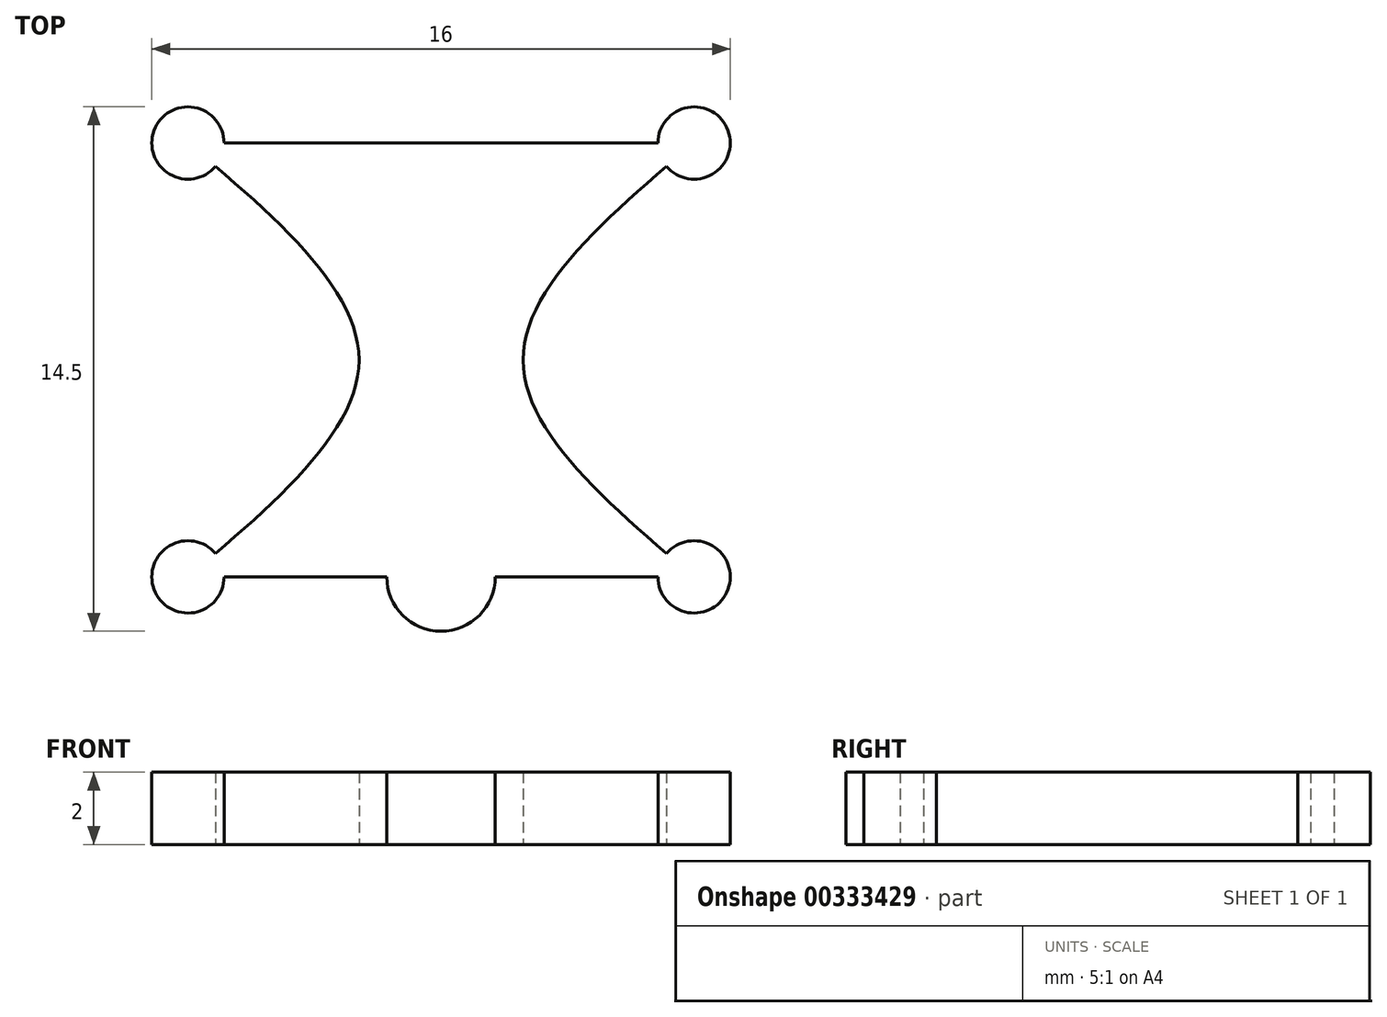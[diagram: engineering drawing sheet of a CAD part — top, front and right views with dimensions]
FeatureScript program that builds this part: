
annotation { "Feature Type Name" : "Feature", "Feature Type Description" : "" }
export const myFeature = defineFeature(function(context is Context, id is Id, definition is map)
    precondition{}
    {
        {
            var Q0;
            Q0=qCreatedBy(makeId("Top.planeOp"),FACE);
            var sketch = newSketch(context, id + "F0", { "sketchPlane" : qUnion([Q0])});
            skLineSegment(sketch, "E0", {"start": v(-7, 0) * mm, "end": v(7, 0) * mm});
            skArc(sketch, "E1", {"start": v(-1.5, 0) * mm, "mid": v(0, 1.5) * mm, "end": v(1.5, 0) * mm});
            skLineSegment(sketch, "E2", {"start": v(0, 0) * mm, "end": v(0, -12) * mm});
            skLineSegment(sketch, "E3", {"start": v(-7, -12) * mm, "end": v(7, -12) * mm});
            skPoint(sketch, "E4", {"position": v(0, -6) * mm});
            skLineSegment(sketch, "E5", {"start": v(-2.27, -6) * mm, "end": v(2.27, -6) * mm});
            skFitSpline(sketch, "E6", {"points": [v(-7, -12) * mm, v(-2.27, -6) * mm, v(-7, 0) * mm], "startDerivative": vector(14.2, 12) * mm, "endDerivative": vector(-14.2, 12) * mm});
            skFitSpline(sketch, "E7", {"points": [v(7, -12) * mm, v(2.27, -6) * mm, v(7, 0) * mm], "startDerivative": vector(-14.2, 12) * mm, "endDerivative": vector(14.2, 12) * mm});
            skCircle(sketch, "E8", {"center": v(-7, 0) * mm, "radius": 1 * mm});
            skCircle(sketch, "E9", {"center": v(-7, -12) * mm, "radius": 1 * mm});
            skCircle(sketch, "E10.MirrorC", {"center": v(7, 0) * mm, "radius": 1 * mm});
            skCircle(sketch, "E11.MirrorC", {"center": v(7, -12) * mm, "radius": 1 * mm});
            skArc(sketch, "E12", {"start": v(-1.5, -12) * mm, "mid": v(0, -13.5) * mm, "end": v(1.5, -12) * mm});
            skSolve(sketch);
        }
        {
            var Q0;
            {var subQ0=sQuery(id+"F0.wireOp",EDGE,"E6");var subQ1=sQuery(id+"F0.wireOp",EDGE,"E0");var subQ2=makeQuery(id+"F0.imprint","INTERSECT",VERTEX,{"derivedFrom":[subQ1,subQ0]});Q0=makeQuery(id+"F0.imprint","IMPRINT",FACE,{"disambiguationData":[TD([[makeQuery(id+"F0.imprint","IMPRINT",EDGE,{"disambiguationData":[TD([[subQ2,-1.0]])],"derivedFrom":subQ1}),1.0]])]});}
            var Q1;
            {var subQ0=sQuery(id+"F0.wireOp",EDGE,"E6");var subQ1=sQuery(id+"F0.wireOp",EDGE,"E0");var subQ2=makeQuery(id+"F0.imprint","INTERSECT",VERTEX,{"derivedFrom":[subQ1,subQ0]});Q1=makeQuery(id+"F0.imprint","IMPRINT",FACE,{"disambiguationData":[TD([[makeQuery(id+"F0.imprint","IMPRINT",EDGE,{"disambiguationData":[TD([[subQ2,-1.0]])],"derivedFrom":subQ1}),-1.0]])]});}
            var Q2;
            {var subQ6=sQuery(id+"F0.wireOp",EDGE,"E0");var subQ10=makeQuery(id+"F0.imprint","INTERSECT",VERTEX,{"disambiguationData":[OD(0.0)],"derivedFrom":[subQ6,sQuery(id+"F0.wireOp",EDGE,"E1")]});Q2=makeQuery(id+"F0.imprint","IMPRINT",FACE,{"disambiguationData":[TD([[makeQuery(id+"F0.imprint","IMPRINT",EDGE,{"disambiguationData":[TD([[subQ10,1.0]])],"derivedFrom":subQ6}),-1.0]])]});}
            var Q3;
            {var subQ0=sQuery(id+"F0.wireOp",EDGE,"E1");Q3=makeQuery(id+"F0.imprint","IMPRINT",FACE,{"disambiguationData":[TD([[makeQuery(id+"F0.imprint","IMPRINT",EDGE,{"derivedFrom":subQ0}),-1.0]])]});}
            var Q4;
            {var subQ5=sQuery(id+"F0.wireOp",EDGE,"E0");var subQ7=makeQuery(id+"F0.imprint","INTERSECT",VERTEX,{"disambiguationData":[OD(1.0)],"derivedFrom":[subQ5,sQuery(id+"F0.wireOp",EDGE,"E1")]});Q4=makeQuery(id+"F0.imprint","IMPRINT",FACE,{"disambiguationData":[TD([[makeQuery(id+"F0.imprint","IMPRINT",EDGE,{"disambiguationData":[TD([[subQ7,1.0]])],"derivedFrom":subQ5}),-1.0]])]});}
            var Q5;
            {var subQ0=sQuery(id+"F0.wireOp",EDGE,"E7");var subQ1=sQuery(id+"F0.wireOp",EDGE,"E0");var subQ2=makeQuery(id+"F0.imprint","INTERSECT",VERTEX,{"derivedFrom":[subQ1,subQ0]});Q5=makeQuery(id+"F0.imprint","IMPRINT",FACE,{"disambiguationData":[TD([[makeQuery(id+"F0.imprint","IMPRINT",EDGE,{"disambiguationData":[TD([[subQ2,1.0]])],"derivedFrom":subQ1}),-1.0]])]});}
            var Q6;
            {var subQ0=sQuery(id+"F0.wireOp",EDGE,"E7");var subQ1=sQuery(id+"F0.wireOp",EDGE,"E0");var subQ2=makeQuery(id+"F0.imprint","INTERSECT",VERTEX,{"derivedFrom":[subQ1,subQ0]});Q6=makeQuery(id+"F0.imprint","IMPRINT",FACE,{"disambiguationData":[TD([[makeQuery(id+"F0.imprint","IMPRINT",EDGE,{"disambiguationData":[TD([[subQ2,1.0]])],"derivedFrom":subQ1}),1.0]])]});}
            var Q7;
            {var subQ0=sQuery(id+"F0.wireOp",EDGE,"E3");var subQ1=sQuery(id+"F0.wireOp",EDGE,"E2");var subQ2=makeQuery(id+"F0.imprint","INTERSECT",VERTEX,{"derivedFrom":[subQ1,subQ0]});Q7=makeQuery(id+"F0.imprint","IMPRINT",FACE,{"disambiguationData":[TD([[makeQuery(id+"F0.imprint","IMPRINT",EDGE,{"disambiguationData":[TD([[subQ2,1.0]])],"derivedFrom":subQ1}),-1.0]])]});}
            var Q8;
            {var subQ3=sQuery(id+"F0.wireOp",EDGE,"E2");var subQ5=sQuery(id+"F0.wireOp",EDGE,"E3");var subQ6=makeQuery(id+"F0.imprint","INTERSECT",VERTEX,{"derivedFrom":[subQ3,subQ5]});Q8=makeQuery(id+"F0.imprint","IMPRINT",FACE,{"disambiguationData":[TD([[makeQuery(id+"F0.imprint","IMPRINT",EDGE,{"disambiguationData":[TD([[subQ6,1.0]])],"derivedFrom":subQ3}),1.0]])]});}
            var Q9;
            {var subQ0=sQuery(id+"F0.wireOp",EDGE,"E6");var subQ1=sQuery(id+"F0.wireOp",EDGE,"E3");var subQ2=makeQuery(id+"F0.imprint","INTERSECT",VERTEX,{"derivedFrom":[subQ1,subQ0]});Q9=makeQuery(id+"F0.imprint","IMPRINT",FACE,{"disambiguationData":[TD([[makeQuery(id+"F0.imprint","IMPRINT",EDGE,{"disambiguationData":[TD([[subQ2,-1.0]])],"derivedFrom":subQ1}),1.0]])]});}
            var Q10;
            {var subQ0=sQuery(id+"F0.wireOp",EDGE,"E6");var subQ1=sQuery(id+"F0.wireOp",EDGE,"E3");var subQ2=makeQuery(id+"F0.imprint","INTERSECT",VERTEX,{"derivedFrom":[subQ1,subQ0]});Q10=makeQuery(id+"F0.imprint","IMPRINT",FACE,{"disambiguationData":[TD([[makeQuery(id+"F0.imprint","IMPRINT",EDGE,{"disambiguationData":[TD([[subQ2,-1.0]])],"derivedFrom":subQ1}),-1.0]])]});}
            var Q11;
            {var subQ2=sQuery(id+"F0.wireOp",EDGE,"E12");Q11=makeQuery(id+"F0.imprint","IMPRINT",FACE,{"disambiguationData":[TD([[makeQuery(id+"F0.imprint","IMPRINT",EDGE,{"derivedFrom":subQ2}),1.0]])]});}
            var Q12;
            {var subQ0=sQuery(id+"F0.wireOp",EDGE,"E7");var subQ1=sQuery(id+"F0.wireOp",EDGE,"E3");var subQ2=makeQuery(id+"F0.imprint","INTERSECT",VERTEX,{"derivedFrom":[subQ1,subQ0]});Q12=makeQuery(id+"F0.imprint","IMPRINT",FACE,{"disambiguationData":[TD([[makeQuery(id+"F0.imprint","IMPRINT",EDGE,{"disambiguationData":[TD([[subQ2,1.0]])],"derivedFrom":subQ1}),1.0]])]});}
            var Q13;
            {var subQ0=sQuery(id+"F0.wireOp",EDGE,"E7");var subQ1=sQuery(id+"F0.wireOp",EDGE,"E3");var subQ2=makeQuery(id+"F0.imprint","INTERSECT",VERTEX,{"derivedFrom":[subQ1,subQ0]});Q13=makeQuery(id+"F0.imprint","IMPRINT",FACE,{"disambiguationData":[TD([[makeQuery(id+"F0.imprint","IMPRINT",EDGE,{"disambiguationData":[TD([[subQ2,1.0]])],"derivedFrom":subQ1}),-1.0]])]});}
            extrude(context, id + "F1", {"entities" : qUnion([Q0, Q1, Q2, Q3, Q4, Q5, Q6, Q7, Q8, Q9, Q10, Q11, Q12, Q13]), "depth" : 2 * mm});
        }
    });
